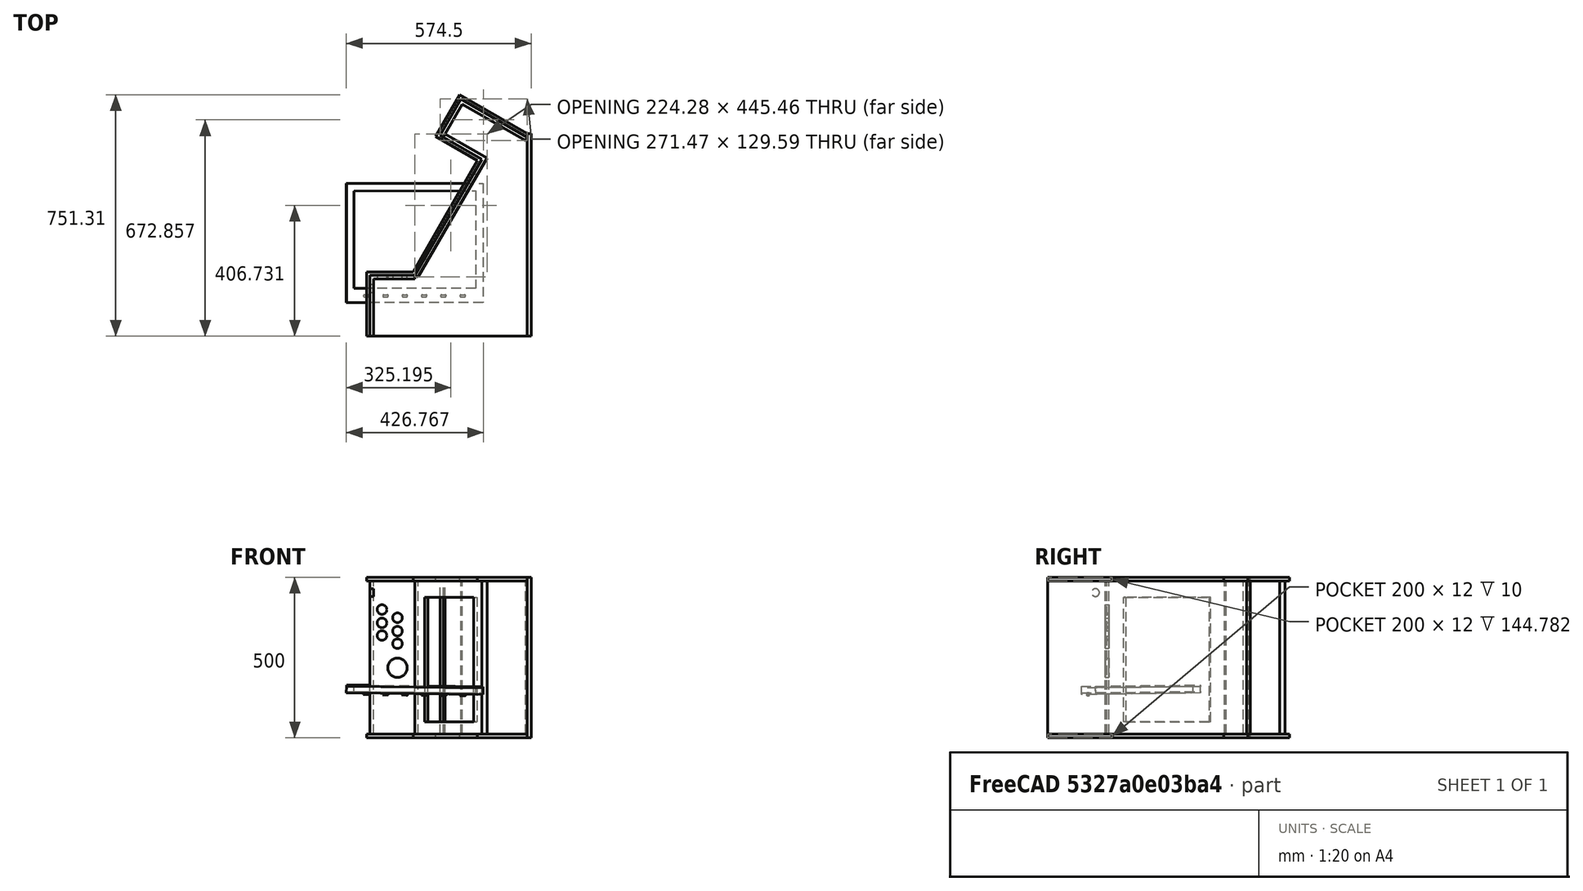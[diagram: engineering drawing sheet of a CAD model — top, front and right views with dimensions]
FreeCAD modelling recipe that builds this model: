
FCSTD DOCUMENT  (FreeCAD 0.18R16131 (Git))
Label: arcadeAvecHaut
License: All rights reserved
LicenseURL: http://en.wikipedia.org/wiki/All_rights_reserved
objects: TechDraw::DrawViewDimension×23, Sketcher::SketchObject×8, PartDesign::Pad×5, TechDraw::DrawViewPart×5, PartDesign::Plane×3, PartDesign::Pocket×3, PartDesign::LinearPattern×2, PartDesign::Body×2, TechDraw::DrawViewAnnotation×2, TechDraw::DrawSVGTemplate×1, TechDraw::DrawPage×1
note: 31 computed .brp shape members not serialized (recipe doc carries the construction recipe); baked Part::Feature solids carry a one-line shape summary decoded from their .brp

FEATURE [Sketcher::SketchObject] Sketch  label="coteGauche"
  MapMode = 5
  Support = -> [XY_Plane]
  sketch-geometry (10):
    g0: LineSegment StartX=-500 StartY=200 StartZ=0 EndX=-500 EndY=0 EndZ=0
    g1: LineSegment StartX=-500 StartY=0 StartZ=0 EndX=0 EndY=0 EndZ=0
    g2: LineSegment StartX=0 StartY=0 StartZ=0 EndX=0 EndY=546.41 EndZ=0
    g3: LineSegment [constr] StartX=0 StartY=546.41 StartZ=0 EndX=-155.218 EndY=546.41 EndZ=0
    g4: LineSegment StartX=-155.218 StartY=546.41 StartZ=0 EndX=-355.218 EndY=200 EndZ=0
    g5: LineSegment StartX=-355.218 StartY=200 StartZ=0 EndX=-500 EndY=200 EndZ=0
    g6: LineSegment StartX=-155.218 StartY=546.41 StartZ=0 EndX=-285.122 EndY=621.41 EndZ=0
    g7: LineSegment StartX=-285.122 StartY=621.41 StartZ=0 EndX=-210.122 EndY=751.314 EndZ=0
    g8: LineSegment StartX=-210.122 StartY=751.314 StartZ=0 EndX=0 EndY=630 EndZ=0
    g9: LineSegment StartX=0 StartY=630 StartZ=0 EndX=0 EndY=546.41 EndZ=0
  constraints (28):
    c: Vertical(g0)
    c: Coincident(g0,g1)
    c: Horizontal(g1)
    c: Coincident(g1,g2)
    c: Vertical(g2)
    c: Coincident(g2,g3)
    c: Horizontal(g3)
    c: Coincident(g3,g4)
    c: Coincident(g5,g0)
    c: DistanceX(g1,g1) = 500
    c: DistanceY(g0,g0) = 200
    c: Horizontal(g5)
    c: Coincident(g4,g5)
    c: Coincident(g1,g-1)
    c: Angle(g4,g3) = 2.0944
    c: Distance(g4) = 400
    c: Coincident(g6,g3)
    c: Coincident(g7,g6)
    c: Coincident(g8,g7)
    c: PointOnObject(g8,g-2)
    c: Coincident(g9,g8)
    c: Coincident(g9,g2)
    c: Perpendicular(g6,g7)
    c: Perpendicular(g7,g8)
    c: Perpendicular(g6,g4)
    c: Distance(g6) = 150
    c: Distance(g7) = 150
    c: DistanceY(g1,g8) = 630
FEATURE [PartDesign::Pad] Pad
  Length = 12
  Length2 = 120
  Profile = -> Sketch
  Type = 0
FEATURE [Sketcher::SketchObject] Sketch002  label="arriere"
  ExternalGeometry = -> [Sketch]
  MapMode = 5
  Placement = pos=(0,0,0) rot=(0.57735,0.57735,0.57735;2.0944rad)
  Support = -> [YZ_Plane]
  sketch-geometry (4):
    g0: LineSegment StartX=0 StartY=0 StartZ=0 EndX=0 EndY=500 EndZ=0
    g1: LineSegment StartX=0 StartY=0 StartZ=0 EndX=630 EndY=1.749e-13 EndZ=0
    g2: LineSegment StartX=630 StartY=1.749e-13 StartZ=0 EndX=630 EndY=500 EndZ=0
    g3: LineSegment StartX=630 StartY=500 StartZ=0 EndX=0 EndY=500 EndZ=0
  constraints (10):
    c: Vertical(g0)
    c: DistanceY(g0,g0) = 500
    c: Coincident(g0,g-1)
    c: Coincident(g1,g-5)
    c: Coincident(g1,g2)
    c: Vertical(g2)
    c: Coincident(g2,g3)
    c: Coincident(g3,g0)
    c: Perpendicular(g2,g3)
    c: Coincident(g1,g0)
FEATURE [PartDesign::Pad] Pad001
  BaseFeature = -> Pad
  Length = 12
  Length2 = 120
  Profile = -> Sketch002
  Type = 0
FEATURE [PartDesign::LinearPattern] LinearPattern  label="coteDroit"
  BaseFeature = -> Pad001
  Direction = -> Z_Axis
  Length = 488
  Occurrences = 2
  Originals = -> [Pad]
FEATURE [Sketcher::SketchObject] Sketch003  label="Interieur"
  ExternalGeometry = -> [Sketch]
  MapMode = 5
  Support = -> [XY_Plane]
  sketch-geometry (39):
    g0: LineSegment StartX=-490 StartY=190 StartZ=0 EndX=-349.445 EndY=190 EndZ=0
    g1: LineSegment StartX=-349.445 StartY=190 StartZ=0 EndX=-141.558 EndY=550.07 EndZ=0
    g2: LineSegment StartX=-131.166 StartY=544.07 StartZ=0 EndX=-261.069 EndY=619.07 EndZ=0
    g3: LineSegment StartX=-271.465 StartY=625.064 StartZ=0 EndX=-206.462 EndY=737.654 EndZ=0
    g4: LineSegment StartX=-255.069 StartY=629.463 StartZ=0 EndX=-125.166 EndY=554.463 EndZ=0
    g5: LineSegment StartX=-131.166 StartY=544.07 StartZ=0 EndX=-339.052 EndY=184 EndZ=0
    g6: LineSegment StartX=-349.445 StartY=178 StartZ=0 EndX=-490 EndY=178 EndZ=0
    g7: LineSegment StartX=-478 StartY=178 StartZ=0 EndX=-478 EndY=0 EndZ=0
    g8: LineSegment StartX=-478 StartY=0 StartZ=0 EndX=-490 EndY=0 EndZ=0
    g9: LineSegment StartX=-490 StartY=0 StartZ=0 EndX=-490 EndY=178 EndZ=0
    g10: LineSegment StartX=-196.069 StartY=731.654 StartZ=0 EndX=0 EndY=618.453 EndZ=0
    g11: LineSegment StartX=-6 StartY=608.061 StartZ=0 EndX=-202.069 EndY=721.261 EndZ=0
    g12: LineSegment StartX=-196.069 StartY=731.654 StartZ=0 EndX=-261.073 EndY=619.064 EndZ=0
    g13: LineSegment [constr] StartX=-263.064 StartY=426.451 StartZ=0 EndX=-129.787 EndY=349.503 EndZ=0
    g14: GeomPoint X=-225.463 Y=404.742 Z=0
    g15: GeomPoint X=-215.071 Y=398.742 Z=0
    g16: LineSegment [constr] StartX=-133.313 StartY=769.102 StartZ=0 EndX=-285.269 EndY=505.906 EndZ=0
    g17: GeomPoint X=-165.218 Y=713.841 Z=0
    g18: GeomPoint X=-171.218 Y=703.449 Z=0
    g19: GeomPoint X=-224.218 Y=611.65 Z=0
    g20: GeomPoint X=-230.218 Y=601.258 Z=0
    g21: GeomPoint X=-235.218 Y=592.598 Z=0
    g22: GeomPoint X=-160.218 Y=722.502 Z=0
    g23: LineSegment [constr] StartX=-317.542 StartY=758.162 StartZ=0 EndX=-98.31 EndY=631.589 EndZ=0
    g24: GeomPoint X=-234.012 Y=709.936 Z=0
    g25: GeomPoint X=-225.351 Y=704.936 Z=0
    g26: GeomPoint X=-214.959 Y=698.936 Z=0
    g27: GeomPoint X=-234.123 Y=409.742 Z=0
    g28: LineSegment StartX=-349.445 StartY=190 StartZ=0 EndX=-349.445 EndY=178 EndZ=0
    g29: LineSegment StartX=-349.445 StartY=190 StartZ=0 EndX=-339.052 EndY=184 EndZ=0
    g30: LineSegment StartX=0 StartY=618.453 StartZ=0 EndX=-6 EndY=608.061 EndZ=0
    g31: LineSegment StartX=-206.462 StartY=737.654 StartZ=0 EndX=-196.069 EndY=731.654 EndZ=0
    g32: LineSegment StartX=-196.069 StartY=731.654 StartZ=0 EndX=-202.069 EndY=721.261 EndZ=0
    g33: LineSegment StartX=-255.069 StartY=629.463 StartZ=0 EndX=-261.069 EndY=619.07 EndZ=0
    g34: LineSegment StartX=-271.465 StartY=625.064 StartZ=0 EndX=-261.073 EndY=619.064 EndZ=0
    g35: LineSegment StartX=-125.166 StartY=554.463 StartZ=0 EndX=-131.166 EndY=544.07 EndZ=0
    g36: LineSegment StartX=-141.558 StartY=550.07 StartZ=0 EndX=-131.166 EndY=544.07 EndZ=0
    g37: LineSegment StartX=-490 StartY=190 StartZ=0 EndX=-490 EndY=178 EndZ=0
    g38: LineSegment StartX=-490 StartY=178 StartZ=0 EndX=-478 EndY=178 EndZ=0
  constraints (98):
    c: Horizontal(g0)
    c: Coincident(g0,g1)
    c: Horizontal(g6)
    c: PointOnObject(g7,g-1)
    c: Vertical(g7)
    c: Coincident(g7,g8)
    c: PointOnObject(g8,g-1)
    c: Coincident(g8,g9)
    c: Vertical(g9)
    c: Parallel(g1,g-3)
    c: Parallel(g5,g1)
    c: Parallel(g-5,g2)
    c: Parallel(g2,g4)
    c: Parallel(g-6,g3)
    c: Parallel(g3,g12)
    c: Parallel(g-7,g10)
    c: Parallel(g10,g11)
    c: PointOnObject(g10,g-2)
    c: DistanceX(g8,g8) = 12
    c: DistanceY(g6,g0) = 12
    c: DistanceX(g-9,g8) = 10
    c: DistanceY(g0,g-9) = 10
    c: Perpendicular(g-3,g13)
    c: PointOnObject(g14,g1)
    c: PointOnObject(g14,g13)
    c: PointOnObject(g15,g13)
    c: PointOnObject(g15,g5)
    c: Distance(g15,g14) = 12
    c: Perpendicular(g16,g-7)
    c: PointOnObject(g17,g10)
    c: PointOnObject(g18,g11)
    c: PointOnObject(g19,g4)
    c: PointOnObject(g20,g2)
    c: PointOnObject(g17,g16)
    c: PointOnObject(g18,g16)
    c: PointOnObject(g19,g16)
    c: PointOnObject(g20,g16)
    c: Distance(g19,g20) = 12
    c: Distance(g18,g17) = 12
    c: PointOnObject(g21,g-5)
    c: PointOnObject(g22,g-7)
    c: PointOnObject(g22,g16)
    c: PointOnObject(g21,g16)
    c: Distance(g20,g21) = 10
    c: Distance(g17,g22) = 10
    c: Perpendicular(g-6,g23)
    c: PointOnObject(g24,g23)
    c: PointOnObject(g25,g23)
    c: PointOnObject(g24,g-6)
    c: PointOnObject(g25,g3)
    c: PointOnObject(g26,g23)
    c: PointOnObject(g26,g12)
    c: Distance(g26,g25) = 12
    c: Distance(g25,g24) = 10
    c: PointOnObject(g27,g13)
    c: PointOnObject(g27,g-3)
    c: Distance(g14,g27) = 10
    c: Distance(g-3) = 400
    c: Distance(g-6) = 150
    c: DistanceX(g-8,g-8) = 144.782
    c: Distance(g-7) = 242.628
    c: Coincident(g28,g0)
    c: Vertical(g28)
    c: Coincident(g29,g0)
    c: Perpendicular(g5,g29)
    c: Coincident(g6,g28)
    c: Coincident(g5,g29)
    c: Coincident(g30,g10)
    c: Perpendicular(g30,g11)
    c: Coincident(g11,g30)
    c: Coincident(g31,g3)
    c: Coincident(g31,g12)
    c: Perpendicular(g3,g31)
    c: Coincident(g32,g10)
    c: Coincident(g32,g11)
    c: Perpendicular(g10,g32,g10) = 4.71239
    c: Coincident(g12,g10)
    c: Coincident(g33,g4)
    c: Perpendicular(g33,g4)
    c: Coincident(g2,g33)
    c: Coincident(g34,g3)
    c: Coincident(g34,g12)
    c: Perpendicular(g34,g3)
    c: PointOnObject(g4,g12)
    c: Coincident(g35,g4)
    c: Coincident(g35,g2)
    c: Perpendicular(g4,g35,g4) = 4.71239
    c: Coincident(g36,g1)
    c: Coincident(g36,g5)
    c: Perpendicular(g36,g1)
    c: Coincident(g5,g2)
    c: Coincident(g37,g0)
    c: Vertical(g37)
    c: Coincident(g6,g37)
    c: Coincident(g38,g9)
    c: Perpendicular(g38,g9)
    c: Coincident(g38,g7)
    c: Coincident(g6,g9)
FEATURE [PartDesign::Pad] Pad002
  BaseFeature = -> LinearPattern
  Length = 488
  Length2 = 100
  Profile = -> Sketch003
  Type = 0
FEATURE [Sketcher::SketchObject] Sketch007
  MapMode = 5
  Support = -> [XY_Plane001]
  sketch-geometry (8):
    g0: LineSegment StartX=-212.5 StartY=185 StartZ=0 EndX=212.5 EndY=185 EndZ=0
    g1: LineSegment StartX=212.5 StartY=185 StartZ=0 EndX=212.5 EndY=-185 EndZ=0
    g2: LineSegment StartX=212.5 StartY=-185 StartZ=0 EndX=-212.5 EndY=-185 EndZ=0
    g3: LineSegment StartX=-212.5 StartY=-185 StartZ=0 EndX=-212.5 EndY=185 EndZ=0
    g4: LineSegment StartX=-189.5 StartY=162 StartZ=0 EndX=189.5 EndY=162 EndZ=0
    g5: LineSegment StartX=189.5 StartY=162 StartZ=0 EndX=189.5 EndY=-141 EndZ=0
    g6: LineSegment StartX=189.5 StartY=-141 StartZ=0 EndX=-189.5 EndY=-141 EndZ=0
    g7: LineSegment StartX=-189.5 StartY=-141 StartZ=0 EndX=-189.5 EndY=162 EndZ=0
  constraints (22):
    c: Coincident(g0,g1)
    c: Coincident(g1,g2)
    c: Coincident(g2,g3)
    c: Coincident(g3,g0)
    c: Horizontal(g2)
    c: Vertical(g1)
    c: Symmetric(g0,g0,g-2)
    c: Symmetric(g0,g2,g-1)
    c: DistanceY(g1,g0) = 370
    c: DistanceX(g0,g0) = 425
    c: Coincident(g4,g5)
    c: Coincident(g5,g6)
    c: Coincident(g6,g7)
    c: Coincident(g7,g4)
    c: Horizontal(g4)
    c: Horizontal(g6)
    c: Vertical(g5)
    c: Vertical(g7)
    c: DistanceY(g4,g0) = 23
    c: DistanceY(g2,g6) = 44
    c: DistanceX(g4,g0) = 23
    c: DistanceX(g0,g4) = 23
FEATURE [PartDesign::Pad] Pad003
  Length = 20
  Length2 = 100
  Profile = -> Sketch007
  Type = 0
FEATURE [Sketcher::SketchObject] Sketch008
  ExternalGeometry = -> [Sketch007]
  MapMode = 5
  Support = -> [XY_Plane001]
  sketch-geometry (5):
    g0: ArcOfCircle CenterX=-155.799 CenterY=-164.625 CenterZ=0 NormalX=0 NormalY=0 NormalZ=1 AngleXU=0 Radius=3.5 StartAngle=1.5708 EndAngle=4.71239
    g1: ArcOfCircle CenterX=-145.799 CenterY=-164.625 CenterZ=0 NormalX=0 NormalY=0 NormalZ=1 AngleXU=0 Radius=3.5 StartAngle=4.71239 EndAngle=7.85398
    g2: LineSegment StartX=-155.799 StartY=-168.125 StartZ=0 EndX=-145.799 EndY=-168.125 EndZ=0
    g3: LineSegment StartX=-155.799 StartY=-161.125 StartZ=0 EndX=-145.799 EndY=-161.125 EndZ=0
    g4: LineSegment [constr] StartX=-243.041 StartY=-164.625 StartZ=0 EndX=239.075 EndY=-164.625 EndZ=0
  constraints (10):
    c: Tangent(g0,g3) = 1.5708
    c: Tangent(g0,g2) = -1.5708
    c: Tangent(g2,g1) = -1.5708
    c: Tangent(g3,g1) = 1.5708
    c: Horizontal(g2)
    c: Equal(g0,g1)
    c: DistanceY(g0,g0) = 7
    c: DistanceX(g0,g1) = 10
    c: Horizontal(g4)
    c: PointOnObject(g1,g4)
FEATURE [PartDesign::Pad] Pad004  label="bouton"
  BaseFeature = -> Pad003
  Length = 5
  Length2 = 100
  Profile = -> Sketch008
  Reversed = true
  Type = 0
FEATURE [PartDesign::LinearPattern] LinearPattern001
  BaseFeature = -> Pad004
  Direction = -> Sketch008 [H_Axis]
  Length = 300
  Occurrences = 6
  Originals = -> [Pad004]
FEATURE [PartDesign::Body] Body001  label="Ecran"
  Group = -> [Sketch007,Pad003,Sketch008,Pad004,LinearPattern001]
  Origin = -> Origin001
  Placement = pos=(-350,290,140) rot=(0.707107,0.707107,0;0.017453rad)
  Tip = -> LinearPattern001
FEATURE [PartDesign::Plane] DatumPlane
  Length = 1051.96
  MapMode = 5
  Placement = pos=(-344.356,198.814,0) rot=(-0.377964,0.654654,0.654654;3.86433rad)
  ResizeMode = 0
  Support = -> [Pad002]
  Width = 646.647
FEATURE [Sketcher::SketchObject] Sketch009  label="Ecran001"
  ExternalGeometry = -> [Pad002,Sketch003]
  MapMode = 5
  Placement = pos=(-344.356,198.814,0) rot=(-0.377964,0.654654,0.654654;3.86433rad)
  Support = -> [DatumPlane]
  sketch-geometry (4):
    g0: LineSegment StartX=-355.596 StartY=438 StartZ=0 EndX=-50 EndY=438 EndZ=0
    g1: LineSegment StartX=-50 StartY=438 StartZ=0 EndX=-50 EndY=50 EndZ=0
    g2: LineSegment StartX=-50 StartY=50 StartZ=0 EndX=-355.596 EndY=50 EndZ=0
    g3: LineSegment StartX=-355.596 StartY=50 StartZ=0 EndX=-355.596 EndY=438 EndZ=0
  constraints (12):
    c: Coincident(g0,g1)
    c: Coincident(g1,g2)
    c: Coincident(g2,g3)
    c: Coincident(g3,g0)
    c: Horizontal(g0)
    c: Horizontal(g2)
    c: Vertical(g1)
    c: Vertical(g3)
    c: DistanceX(g-5,g2) = 50
    c: DistanceY(g-5,g2) = 50
    c: DistanceX(g1,g-1) = 50
    c: DistanceY(g3,g3) = 388
FEATURE [PartDesign::Plane] DatumPlane001
  Length = 614.2
  MapMode = 5
  Placement = pos=(0,190,0) rot=(0,0.707107,0.707107;3.14159rad)
  ResizeMode = 0
  Width = 612.2
FEATURE [Sketcher::SketchObject] Sketch011  label="manette"
  MapMode = 5
  Placement = pos=(0,190,0) rot=(0,0.707107,0.707107;3.14159rad)
  Support = -> [DatumPlane001]
  sketch-geometry (9):
    g0: Circle CenterX=403.605 CenterY=218.326 CenterZ=0 NormalX=0 NormalY=0 NormalZ=1 AngleXU=0 Radius=30
    g1: Circle CenterX=403.605 CenterY=293.285 CenterZ=0 NormalX=0 NormalY=0 NormalZ=1 AngleXU=0 Radius=15
    g2: Circle CenterX=403.605 CenterY=332.252 CenterZ=0 NormalX=0 NormalY=0 NormalZ=1 AngleXU=0 Radius=15
    g3: Circle CenterX=403.605 CenterY=373.913 CenterZ=0 NormalX=0 NormalY=0 NormalZ=1 AngleXU=0 Radius=15
    g4: Circle CenterX=451.661 CenterY=357.829 CenterZ=0 NormalX=0 NormalY=0 NormalZ=1 AngleXU=0 Radius=15
    g5: Circle CenterX=451.661 CenterY=318.863 CenterZ=0 NormalX=0 NormalY=0 NormalZ=1 AngleXU=0 Radius=15
    g6: Circle CenterX=451.661 CenterY=399.49 CenterZ=0 NormalX=0 NormalY=0 NormalZ=1 AngleXU=0 Radius=15
    g7: LineSegment [constr] StartX=403.605 StartY=120.684 StartZ=0 EndX=403.605 EndY=527.697 EndZ=0
    g8: LineSegment [constr] StartX=451.661 StartY=111.599 StartZ=0 EndX=451.661 EndY=538.599 EndZ=0
  constraints (16):
    c: Radius(g0) = 30
    c: Radius(g1) = 15
    c: Radius(g2) = 15
    c: Radius(g3) = 15
    c: Radius(g5) = 15
    c: Radius(g4) = 15
    c: Radius(g6) = 15
    c: Vertical(g7)
    c: Vertical(g8)
    c: PointOnObject(g0,g7)
    c: PointOnObject(g1,g7)
    c: PointOnObject(g2,g7)
    c: PointOnObject(g3,g7)
    c: PointOnObject(g5,g8)
    c: PointOnObject(g4,g8)
    c: PointOnObject(g6,g8)
FEATURE [PartDesign::Pocket] Pocket004
  BaseFeature = -> Pad002
  Length = 5
  Length2 = 100
  Profile = -> Sketch011
  Type = 1
FEATURE [PartDesign::Plane] DatumPlane002
  Length = 885.937
  MapMode = 5
  Placement = pos=(-490,0,0) rot=(0.57735,-0.57735,-0.57735;2.0944rad)
  ResizeMode = 0
  Support = -> [Pocket004]
  Width = 634.623
FEATURE [Sketcher::SketchObject] Sketch012  label="credit"
  MapMode = 5
  Placement = pos=(-490,0,0) rot=(0.57735,-0.57735,-0.57735;2.0944rad)
  Support = -> [DatumPlane002]
  sketch-geometry (1):
    g0: Circle CenterX=-148.426 CenterY=452.331 CenterZ=0 NormalX=0 NormalY=0 NormalZ=1 AngleXU=0 Radius=12
  constraints (1):
    c: Radius(g0) = 12
FEATURE [PartDesign::Pocket] Pocket
  BaseFeature = -> Pocket004
  Length = 0
  Length2 = 100
  Profile = -> Sketch012
  Type = 2
FEATURE [TechDraw::DrawSVGTemplate] Template001
  Height = 210
  Orientation = 1
  Width = 297
FEATURE [TechDraw::DrawViewPart] View  label="Gauche"
  CoarseView = false
  Direction = (0,0,1)
  Focus = 100
  HardHidden = false
  IsoCount = 0
  IsoHidden = false
  IsoVisible = false
  LockPosition = false
  Perspective = false
  Rotation = 0
  Scale = 0.1
  ScaleType = 2
  SeamHidden = false
  SeamVisible = false
  SmoothHidden = false
  SmoothVisible = false
  Source = -> [Pad]
  X = 52.2904
  Y = 139.376
FEATURE [TechDraw::DrawViewDimension] Dimension002
  Arbitrary = false
  FormatSpec = %.2f
  LockPosition = false
  MeasureType = 1
  OverTolerance = 0
  References2D = -> [View]
  Rotation = 0
  ScaleType = 0
  Type = 1
  UnderTolerance = 0
  X = 1.2397
  Y = -46.4916
FEATURE [TechDraw::DrawViewDimension] Dimension004
  Arbitrary = false
  FormatSpec = %.2f
  LockPosition = false
  MeasureType = 1
  OverTolerance = 0
  References2D = -> [View]
  Rotation = 0
  ScaleType = 0
  Type = 1
  UnderTolerance = 0
  X = -38.0185
  Y = -1.42832
FEATURE [TechDraw::DrawViewDimension] Dimension005
  Arbitrary = false
  FormatSpec = %.2f
  LockPosition = false
  MeasureType = 1
  OverTolerance = 0
  References2D = -> [View]
  Rotation = 0
  ScaleType = 0
  Type = 0
  UnderTolerance = 0
  X = 2.22497
  Y = -2.30528
FEATURE [TechDraw::DrawViewDimension] Dimension006
  Arbitrary = false
  FormatSpec = %.2f
  LockPosition = false
  MeasureType = 1
  OverTolerance = 0
  References2D = -> [View]
  Rotation = 0
  ScaleType = 0
  Type = 2
  UnderTolerance = 0
  X = 46.9743
  Y = -2.97556
FEATURE [TechDraw::DrawViewDimension] Dimension007
  Arbitrary = false
  FormatSpec = %.2f
  LockPosition = false
  MeasureType = 1
  OverTolerance = 0
  References2D = -> [View]
  Rotation = 0
  ScaleType = 0
  Type = 1
  UnderTolerance = 0
  X = 40.5884
  Y = 56.5644
FEATURE [TechDraw::DrawViewDimension] Dimension008
  Arbitrary = false
  FormatSpec = %.2f
  LockPosition = false
  MeasureType = 1
  OverTolerance = 0
  References2D = -> [View]
  Rotation = 0
  ScaleType = 0
  Type = 2
  UnderTolerance = 0
  X = 59.1292
  Y = -4.46353
FEATURE [TechDraw::DrawViewDimension] Dimension009
  Arbitrary = false
  FormatSpec = %.2f
  LockPosition = false
  MeasureType = 1
  OverTolerance = 0
  References2D = -> [View]
  Rotation = 0
  ScaleType = 0
  Type = 2
  UnderTolerance = 0
  X = -47.4876
  Y = 55.7916
FEATURE [TechDraw::DrawViewDimension] Dimension010
  Arbitrary = false
  FormatSpec = %.2f
  LockPosition = false
  MeasureType = 1
  OverTolerance = 0
  References2D = -> [View]
  Rotation = 0
  ScaleType = 0
  Type = 2
  UnderTolerance = 0
  X = 34.4065
  Y = -2.69152
FEATURE [TechDraw::DrawViewDimension] Dimension011
  Arbitrary = false
  FormatSpec = %.2f
  LockPosition = false
  MeasureType = 1
  OverTolerance = 0
  References2D = -> [View]
  Rotation = 0
  ScaleType = 0
  Type = 1
  UnderTolerance = 0
  X = 40.2434
  Y = 45.5732
FEATURE [TechDraw::DrawViewDimension] Dimension012
  Arbitrary = false
  FormatSpec = %.2f
  LockPosition = false
  MeasureType = 1
  OverTolerance = 0
  References2D = -> [View]
  Rotation = 0
  ScaleType = 0
  Type = 1
  UnderTolerance = 0
  X = 39.9285
  Y = 65.8633
FEATURE [TechDraw::DrawViewDimension] Dimension013
  Arbitrary = false
  FormatSpec = %.2f
  LockPosition = false
  MeasureType = 1
  OverTolerance = 0
  References2D = -> [View]
  Rotation = 0
  ScaleType = 0
  Type = 2
  UnderTolerance = 0
  X = -39.4563
  Y = -54.3469
FEATURE [TechDraw::DrawViewDimension] Dimension016
  Arbitrary = false
  FormatSpec = %.2f
  LockPosition = false
  MeasureType = 1
  OverTolerance = 0
  References2D = -> [View]
  Rotation = 0
  ScaleType = 0
  Type = 0
  UnderTolerance = 0
  X = -25.6294
  Y = 14.8167
FEATURE [TechDraw::DrawViewAnnotation] Annotation  label="Dimensions"
  Font = Times New Roman
  LineSpace = 80
  LockPosition = false
  MaxWidth = -1
  Rotation = 0
  ScaleType = 0
  Text = : (2) 50,0x75,1 | : (1) 50,0x63,0 | : (1) 47,6x13,0 | : (1) 47,6x17,8 | : (1) 47,6x14,1 | : (1) 47,6x15,0 | : (1) 47,6x22,6 | : (1) 47,6x41,6
  TextSize = 4
  TextStyle = 0
  X = 264.695
  Y = 36.1066
FEATURE [TechDraw::DrawViewAnnotation] Annotation001  label="Description"
  Font = Times New Roman
  LineSpace = 80
  LockPosition = false
  MaxWidth = -1
  Rotation = 0
  ScaleType = 0
  Text = Cotes | Arriere | Face Haut | Face bas | Face Hori | Face Dessous | Dessus | Ecran
  TextSize = 4
  TextStyle = 0
  X = 224.235
  Y = 36.6774
FEATURE [PartDesign::Pocket] Pocket005
  BaseFeature = -> Pocket
  Length = 5
  Length2 = 100
  Profile = -> Sketch009
  Type = 2
FEATURE [PartDesign::Body] Body  label="socle"
  Group = -> [Sketch,Pad,Sketch002,Pad001,LinearPattern,Sketch003,Pad002,DatumPlane,Sketch009,DatumPlane001,Sketch011,Pocket004,DatumPlane002,Sketch012,Pocket,Pocket005]
  Origin = -> Origin
  Tip = -> Pocket005
FEATURE [TechDraw::DrawViewPart] View005  label="Devant"
  CoarseView = false
  Direction = (-1,0,0)
  Focus = 100
  HardHidden = false
  IsoCount = 0
  IsoHidden = false
  IsoVisible = false
  LockPosition = false
  Perspective = false
  Rotation = 90
  Scale = 0.1
  ScaleType = 2
  SeamHidden = false
  SeamVisible = false
  SmoothHidden = false
  SmoothVisible = false
  Source = -> [Pocket005]
  X = 153.754
  Y = 140.395
FEATURE [TechDraw::DrawViewDimension] Dimension
  Arbitrary = false
  FormatSpec = %.2f
  LockPosition = false
  MeasureType = 1
  OverTolerance = 0
  References2D = -> [View005]
  Rotation = 0
  ScaleType = 0
  Type = 1
  UnderTolerance = 0
  X = 2.7101
  Y = -51.8326
FEATURE [TechDraw::DrawViewPart] View007  label="Interieur001"
  CoarseView = false
  Direction = (0,0,1)
  Focus = 100
  HardHidden = false
  IsoCount = 0
  IsoHidden = false
  IsoVisible = false
  LockPosition = false
  Perspective = false
  Rotation = 0
  Scale = 0.1
  ScaleType = 0
  SeamHidden = false
  SeamVisible = false
  SmoothHidden = false
  SmoothVisible = false
  Source = -> [Sketch003]
  X = 231.044
  Y = 141.35
FEATURE [TechDraw::DrawViewDimension] Dimension017
  Arbitrary = false
  FormatSpec = %.2f
  LockPosition = false
  MeasureType = 1
  OverTolerance = 0
  References2D = -> [View007]
  Rotation = 0
  ScaleType = 0
  Type = 2
  UnderTolerance = 0
  X = -38.1342
  Y = -27.374
FEATURE [TechDraw::DrawViewDimension] Dimension018
  Arbitrary = false
  FormatSpec = %.2f
  LockPosition = false
  MeasureType = 1
  OverTolerance = 0
  References2D = -> [View007]
  Rotation = 0
  ScaleType = 0
  Type = 1
  UnderTolerance = 0
  X = -18.0809
  Y = -5.34406
FEATURE [TechDraw::DrawViewDimension] Dimension019
  Arbitrary = false
  FormatSpec = %.2f
  LockPosition = false
  MeasureType = 1
  OverTolerance = 0
  References2D = -> [View007]
  Rotation = 0
  ScaleType = 0
  Type = 0
  UnderTolerance = 0
  X = 7.31928
  Y = -4.37466
FEATURE [TechDraw::DrawViewDimension] Dimension021
  Arbitrary = false
  FormatSpec = %.2f
  LockPosition = false
  MeasureType = 1
  OverTolerance = 0
  References2D = -> [View007]
  Rotation = 0
  ScaleType = 0
  Type = 0
  UnderTolerance = 0
  X = -27.2664
  Y = 48.0649
FEATURE [TechDraw::DrawViewDimension] Dimension022
  Arbitrary = false
  FormatSpec = %.2f
  LockPosition = false
  MeasureType = 1
  OverTolerance = 0
  References2D = -> [View007]
  Rotation = 0
  ScaleType = 0
  Type = 0
  UnderTolerance = 0
  X = 19.079
  Y = 40.9701
FEATURE [TechDraw::DrawViewDimension] Dimension023
  Arbitrary = false
  FormatSpec = %.2f
  LockPosition = false
  MeasureType = 1
  OverTolerance = 0
  References2D = -> [View007]
  Rotation = 0
  ScaleType = 0
  Type = 1
  UnderTolerance = 0
  X = -6.97894
  Y = -45.0389
FEATURE [TechDraw::DrawViewDimension] Dimension024
  Arbitrary = false
  FormatSpec = %.2f
  LockPosition = false
  MeasureType = 1
  OverTolerance = 0
  References2D = -> [View007]
  Rotation = 0
  ScaleType = 0
  Type = 0
  UnderTolerance = 0
  X = 0.017436
  Y = 16.6939
FEATURE [TechDraw::DrawViewPart] View008  label="3D"
  CoarseView = true
  Direction = (-0.776,0.389,0.496)
  Focus = 100
  HardHidden = true
  IsoCount = 0
  IsoHidden = true
  IsoVisible = false
  LockPosition = false
  Perspective = true
  Rotation = 90
  Scale = 0.09
  ScaleType = 0
  SeamHidden = false
  SeamVisible = false
  SmoothHidden = false
  SmoothVisible = false
  Source = -> [Pocket005]
  X = 61.2755
  Y = 45.4138
FEATURE [TechDraw::DrawViewPart] View009  label="Dessus"
  CoarseView = false
  Direction = (0,1,0)
  Focus = 100
  HardHidden = false
  IsoCount = 0
  IsoHidden = false
  IsoVisible = false
  LockPosition = false
  Perspective = false
  Rotation = 90
  Scale = 0.1
  ScaleType = 0
  SeamHidden = false
  SeamVisible = false
  SmoothHidden = false
  SmoothVisible = false
  Source = -> [Pocket005]
  X = 154.593
  Y = 47.6741
FEATURE [TechDraw::DrawViewDimension] Dimension025
  Arbitrary = false
  FormatSpec = %.2f
  LockPosition = false
  MeasureType = 1
  OverTolerance = 0
  References2D = -> [View]
  Rotation = 0
  ScaleType = 0
  Type = 2
  UnderTolerance = 0
  X = 33.5959
  Y = 29.8129
FEATURE [TechDraw::DrawViewDimension] Dimension026
  Arbitrary = false
  FormatSpec = %.2f
  LockPosition = false
  MeasureType = 1
  OverTolerance = 0
  References2D = -> [View]
  Rotation = 0
  ScaleType = 0
  Type = 2
  UnderTolerance = 0
  X = 46.8955
  Y = 30.3923
FEATURE [TechDraw::DrawViewDimension] Dimension027
  Arbitrary = false
  FormatSpec = %.2f
  LockPosition = false
  MeasureType = 1
  OverTolerance = 0
  References2D = -> [View]
  Rotation = 0
  ScaleType = 0
  Type = 0
  UnderTolerance = 0
  X = -22.471
  Y = 63.4721
FEATURE [TechDraw::DrawPage] Page001
  KeepUpdated = true
  ProjectionType = 0
  Template = -> Template001
  Views = -> [View,Dimension002,Dimension004,Dimension005,Dimension006,Dimension007,Dimension008,Dimension009,Dimension010,Dimension011,Dimension012,Dimension013,Dimension016,Annotation,Annotation001,View005,Dimension,View007,Dimension017,Dimension018,Dimension019,Dimension021,Dimension022,Dimension023,Dimension024,View008,View009,Dimension025,Dimension026,Dimension027]
